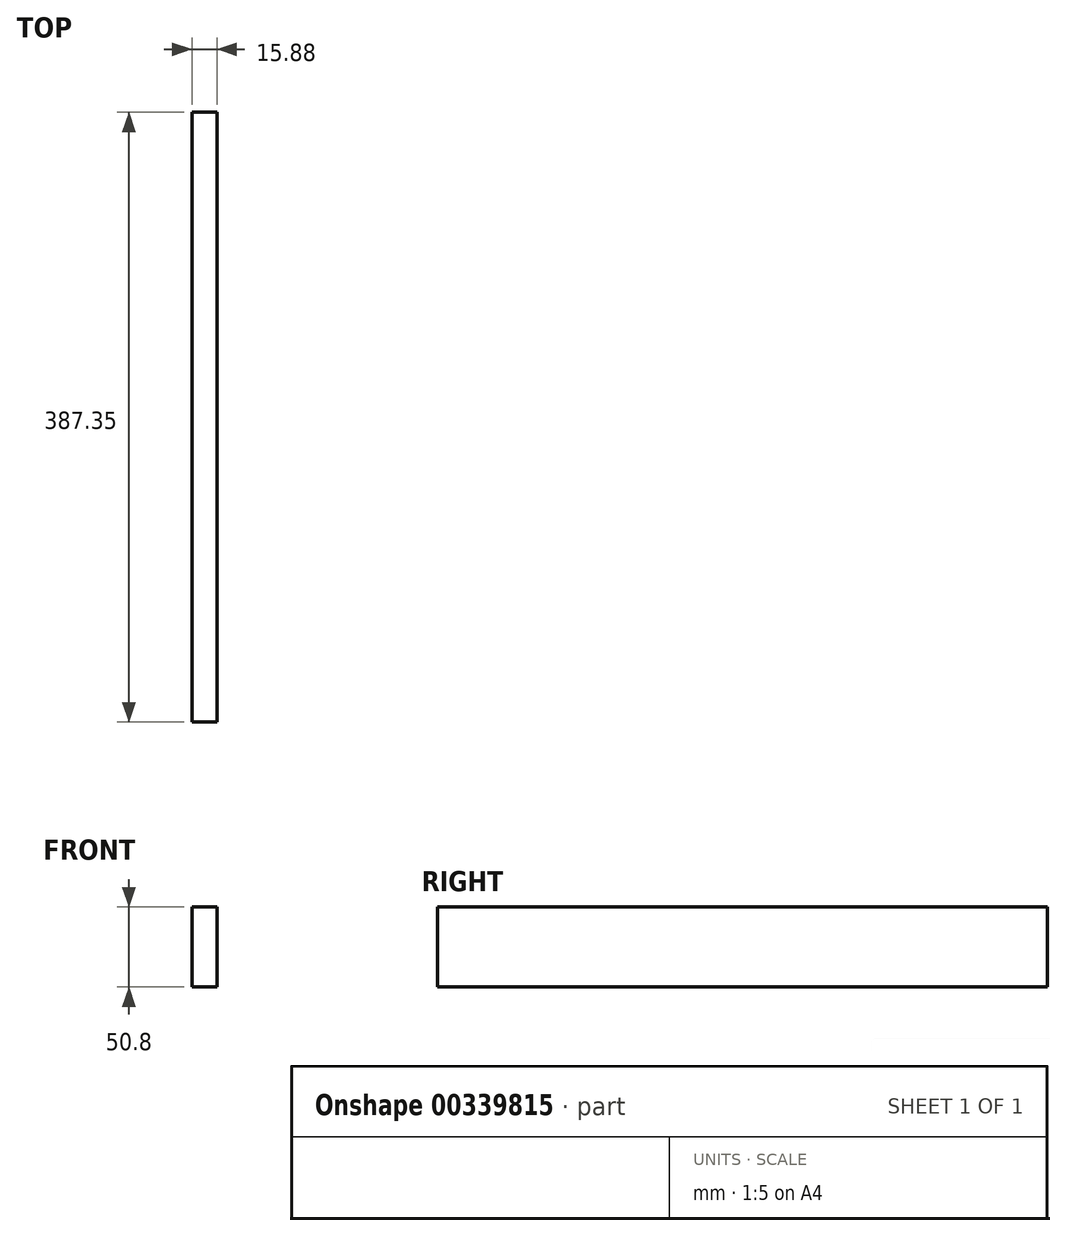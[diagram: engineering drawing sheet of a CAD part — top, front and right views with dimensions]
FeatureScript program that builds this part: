
annotation { "Feature Type Name" : "Feature", "Feature Type Description" : "" }
export const myFeature = defineFeature(function(context is Context, id is Id, definition is map)
    precondition{}
    {
        {
            var Q0;
            Q0=qCreatedBy(makeId("Right.planeOp"),FACE);
            var sketch = newSketch(context, id + "F0", { "sketchPlane" : qUnion([Q0])});
            skLineSegment(sketch, "E0.bottom", {"start": v(-140.88, 26.13) * mm, "end": v(246.47, 26.13) * mm});
            skLineSegment(sketch, "E0.top", {"start": v(-140.88, -24.67) * mm, "end": v(246.47, -24.67) * mm});
            skLineSegment(sketch, "E0.left", {"start": v(-140.88, 26.13) * mm, "end": v(-140.88, -24.67) * mm});
            skLineSegment(sketch, "E0.right", {"start": v(246.47, 26.13) * mm, "end": v(246.47, -24.67) * mm});
            skSolve(sketch);
        }
        {
            var Q0;
            Q0 = qSketchRegion(id + "F0", true);
            extrude(context, id + "F1", {"entities" : qUnion([Q0]), "depth" : 15.88 * mm});
        }
    });
